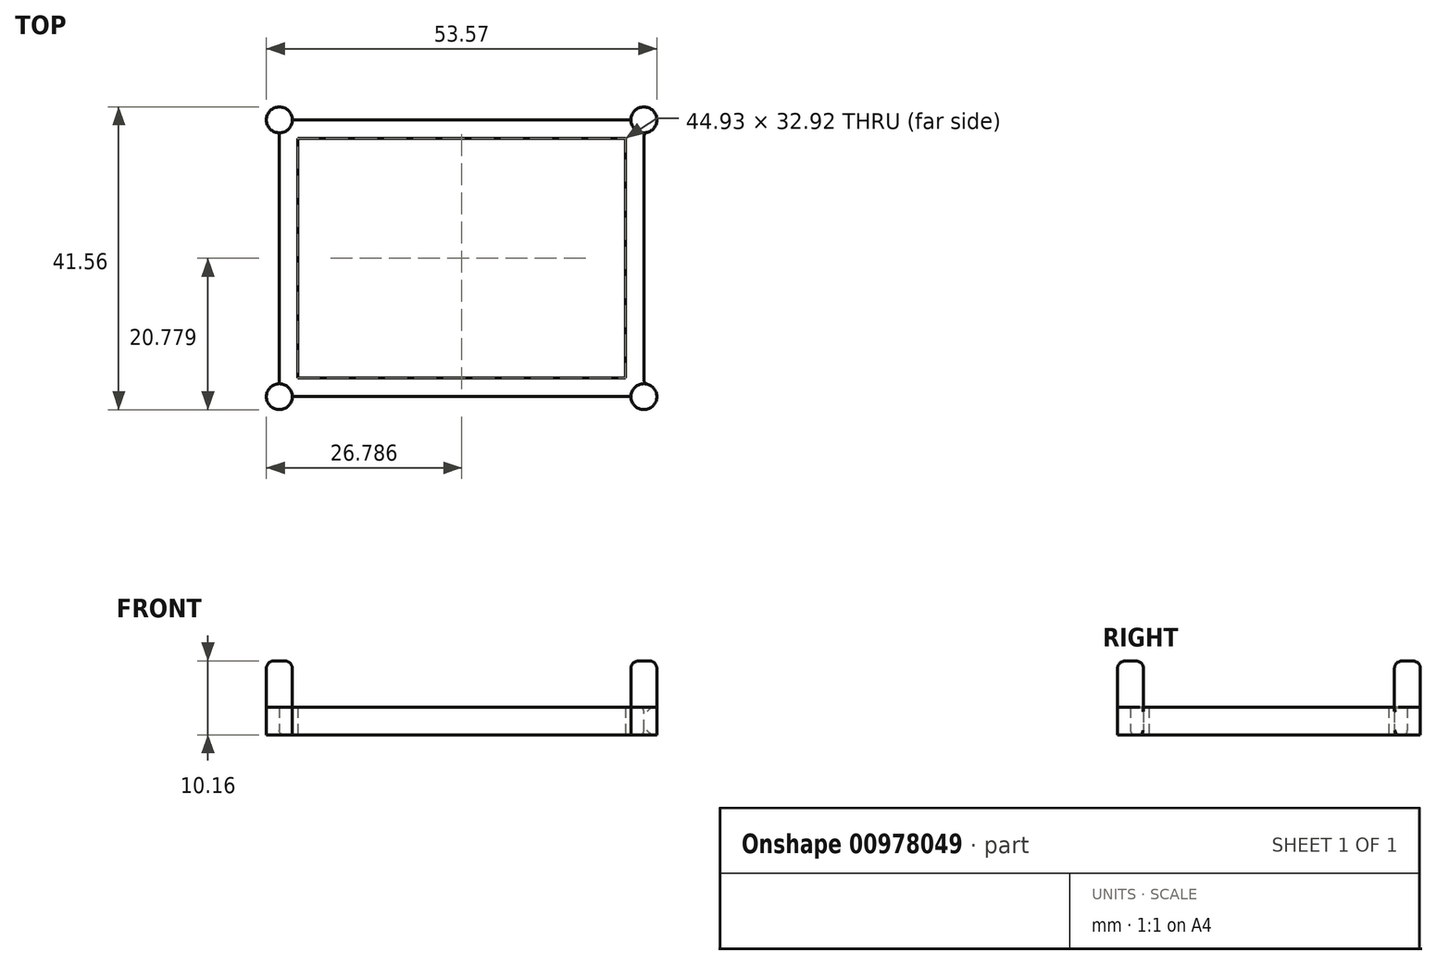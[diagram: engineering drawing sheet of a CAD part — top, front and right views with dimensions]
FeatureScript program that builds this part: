
annotation { "Feature Type Name" : "Feature", "Feature Type Description" : "" }
export const myFeature = defineFeature(function(context is Context, id is Id, definition is map)
    precondition{}
    {
        {
            var Q0;
            Q0=qCreatedBy(makeId("Top.planeOp"),FACE);
            var sketch = newSketch(context, id + "F0", { "sketchPlane" : qUnion([Q0])});
            skLineSegment(sketch, "E0.bottom", {"start": v(0, 0) * mm, "end": v(50.01, 0) * mm});
            skLineSegment(sketch, "E0.top", {"start": v(0, 38) * mm, "end": v(50.01, 38) * mm});
            skLineSegment(sketch, "E0.left", {"start": v(0, 0) * mm, "end": v(0, 38) * mm});
            skLineSegment(sketch, "E0.right", {"start": v(50.01, 0) * mm, "end": v(50.01, 38) * mm});
            skCircle(sketch, "E1", {"center": v(50.01, 38) * mm, "radius": 1.78 * mm});
            skCircle(sketch, "E2", {"center": v(0, 38) * mm, "radius": 1.78 * mm});
            skCircle(sketch, "E3", {"center": v(0, 0) * mm, "radius": 1.78 * mm});
            skCircle(sketch, "E4", {"center": v(50.01, 0) * mm, "radius": 1.78 * mm});
            skSolve(sketch);
        }
        {
            var Q0;
            {var subQ0=sQuery(id+"F0.wireOp",EDGE,"E2");var subQ1=sQuery(id+"F0.wireOp",EDGE,"E0.top");var subQ2=makeQuery(id+"F0.imprint","INTERSECT",VERTEX,{"derivedFrom":[subQ1,subQ0]});Q0=makeQuery(id+"F0.imprint","IMPRINT",FACE,{"disambiguationData":[TD([[makeQuery(id+"F0.imprint","IMPRINT",EDGE,{"disambiguationData":[TD([[subQ2,1.0]])],"derivedFrom":subQ1}),1.0]])]});}
            var Q1;
            {var subQ0=sQuery(id+"F0.wireOp",EDGE,"E2");var subQ1=sQuery(id+"F0.wireOp",EDGE,"E0.top");var subQ2=makeQuery(id+"F0.imprint","INTERSECT",VERTEX,{"derivedFrom":[subQ1,subQ0]});Q1=makeQuery(id+"F0.imprint","IMPRINT",FACE,{"disambiguationData":[TD([[makeQuery(id+"F0.imprint","IMPRINT",EDGE,{"disambiguationData":[TD([[subQ2,1.0]])],"derivedFrom":subQ1}),-1.0]])]});}
            var Q2;
            {var subQ0=sQuery(id+"F0.wireOp",EDGE,"E3");var subQ1=sQuery(id+"F0.wireOp",EDGE,"E0.bottom");var subQ2=makeQuery(id+"F0.imprint","INTERSECT",VERTEX,{"derivedFrom":[subQ1,subQ0]});Q2=makeQuery(id+"F0.imprint","IMPRINT",FACE,{"disambiguationData":[TD([[makeQuery(id+"F0.imprint","IMPRINT",EDGE,{"disambiguationData":[TD([[subQ2,1.0]])],"derivedFrom":subQ1}),-1.0]])]});}
            var Q3;
            {var subQ0=sQuery(id+"F0.wireOp",EDGE,"E3");var subQ1=sQuery(id+"F0.wireOp",EDGE,"E0.bottom");var subQ2=makeQuery(id+"F0.imprint","INTERSECT",VERTEX,{"derivedFrom":[subQ1,subQ0]});Q3=makeQuery(id+"F0.imprint","IMPRINT",FACE,{"disambiguationData":[TD([[makeQuery(id+"F0.imprint","IMPRINT",EDGE,{"disambiguationData":[TD([[subQ2,1.0]])],"derivedFrom":subQ1}),1.0]])]});}
            var Q4;
            {var subQ0=sQuery(id+"F0.wireOp",EDGE,"E0.right");var subQ1=sQuery(id+"F0.wireOp",EDGE,"E0.bottom");var subQ2=makeQuery(id+"F0.imprint","INTERSECT",VERTEX,{"derivedFrom":[subQ1,subQ0]});Q4=makeQuery(id+"F0.imprint","IMPRINT",FACE,{"disambiguationData":[TD([[makeQuery(id+"F0.imprint","IMPRINT",EDGE,{"disambiguationData":[TD([[subQ2,1.0]])],"derivedFrom":subQ1}),1.0]])]});}
            var Q5;
            {var subQ0=sQuery(id+"F0.wireOp",EDGE,"E0.right");var subQ1=sQuery(id+"F0.wireOp",EDGE,"E0.bottom");var subQ2=makeQuery(id+"F0.imprint","INTERSECT",VERTEX,{"derivedFrom":[subQ1,subQ0]});Q5=makeQuery(id+"F0.imprint","IMPRINT",FACE,{"disambiguationData":[TD([[makeQuery(id+"F0.imprint","IMPRINT",EDGE,{"disambiguationData":[TD([[subQ2,1.0]])],"derivedFrom":subQ1}),-1.0]])]});}
            var Q6;
            {var subQ0=sQuery(id+"F0.wireOp",EDGE,"E0.right");var subQ1=sQuery(id+"F0.wireOp",EDGE,"E0.top");var subQ2=makeQuery(id+"F0.imprint","INTERSECT",VERTEX,{"derivedFrom":[subQ1,subQ0]});Q6=makeQuery(id+"F0.imprint","IMPRINT",FACE,{"disambiguationData":[TD([[makeQuery(id+"F0.imprint","IMPRINT",EDGE,{"disambiguationData":[TD([[subQ2,1.0]])],"derivedFrom":subQ1}),-1.0]])]});}
            var Q7;
            {var subQ0=sQuery(id+"F0.wireOp",EDGE,"E0.right");var subQ1=sQuery(id+"F0.wireOp",EDGE,"E0.top");var subQ2=makeQuery(id+"F0.imprint","INTERSECT",VERTEX,{"derivedFrom":[subQ1,subQ0]});Q7=makeQuery(id+"F0.imprint","IMPRINT",FACE,{"disambiguationData":[TD([[makeQuery(id+"F0.imprint","IMPRINT",EDGE,{"disambiguationData":[TD([[subQ2,1.0]])],"derivedFrom":subQ1}),1.0]])]});}
            extrude(context, id + "F1", {"entities" : qUnion([Q0, Q1, Q2, Q3, Q4, Q5, Q6, Q7]), "depth" : 10.16 * mm, "offsetDistance" : 25.4 * mm});
        }
        {
            var Q0;
            Q0 = qSketchRegion(id + "F0", true);
            extrude(context, id + "F2", {"entities" : qUnion([Q0]), "depth" : 3.8 * mm, "offsetDistance" : 25.4 * mm});
        }
        {
            var Q0;
            Q0=makeQuery(id+"F2.opExtrude","CAP_FACE",FACE,{"disambiguationData":[OSD([sQuery(id+"F0.wireOp",EDGE,"E0.bottom"),sQuery(id+"F0.wireOp",EDGE,"E0.top"),sQuery(id+"F0.wireOp",EDGE,"E0.left"),sQuery(id+"F0.wireOp",EDGE,"E0.right"),sQuery(id+"F0.wireOp",EDGE,"E1"),sQuery(id+"F0.wireOp",EDGE,"E2"),sQuery(id+"F0.wireOp",EDGE,"E3"),sQuery(id+"F0.wireOp",EDGE,"E4")])],"isStart":true});
            var sketch = newSketch(context, id + "F3", { "sketchPlane" : qUnion([Q0])});
            skLineSegment(sketch, "E5.bottom", {"start": v(2.54, -2.54) * mm, "end": v(47.47, -2.54) * mm});
            skLineSegment(sketch, "E5.top", {"start": v(2.54, -35.46) * mm, "end": v(47.47, -35.46) * mm});
            skLineSegment(sketch, "E5.left", {"start": v(2.54, -2.54) * mm, "end": v(2.54, -35.46) * mm});
            skLineSegment(sketch, "E5.right", {"start": v(47.47, -2.54) * mm, "end": v(47.47, -35.46) * mm});
            skSolve(sketch);
        }
        {
            var Q0;
            Q0 = qSketchRegion(id + "F3", true);
            extrude(context, id + "F4", {"entities" : qUnion([Q0]), "operationType" : NewBodyOperationType.REMOVE, "oppositeDirection" : true, "depth" : 25.4 * mm, "offsetDistance" : 25.4 * mm});
        }
        {
            var Q0;
            Q0=makeQuery(id+"F1.opExtrude","CAP_EDGE",EDGE,{"disambiguationData":[OSD([sQuery(id+"F0.wireOp",EDGE,"E3")])],"isStart":false});
            var Q1;
            Q1=makeQuery(id+"F1.opExtrude","CAP_EDGE",EDGE,{"disambiguationData":[OSD([sQuery(id+"F0.wireOp",EDGE,"E2")])],"isStart":false});
            var Q2;
            Q2=makeQuery(id+"F1.opExtrude","CAP_EDGE",EDGE,{"disambiguationData":[OSD([sQuery(id+"F0.wireOp",EDGE,"E1")])],"isStart":false});
            var Q3;
            Q3=makeQuery(id+"F1.opExtrude","CAP_EDGE",EDGE,{"disambiguationData":[OSD([sQuery(id+"F0.wireOp",EDGE,"E4")])],"isStart":false});
            fillet(context, id + "F5", {"entities" : qUnion([Q0, Q1, Q2, Q3]), "tangentPropagation" : true, "radius" : 1.04 * mm, "defaultsChanged" : false, "vertexSettings" : [], "allowEdgeOverflow" : false});
        }
        {
            var Q0;
            Q0=makeQuery(id+"F2.opExtrude","CAP_EDGE",EDGE,{"disambiguationData":[OSD([sQuery(id+"F0.wireOp",EDGE,"E0.bottom")])],"isStart":true});
            var Q1;
            Q1=makeQuery(id+"F2.opExtrude","CAP_EDGE",EDGE,{"disambiguationData":[OSD([sQuery(id+"F0.wireOp",EDGE,"E0.left")])],"isStart":true});
            var Q2;
            Q2=makeQuery(id+"F2.opExtrude","CAP_EDGE",EDGE,{"disambiguationData":[OSD([sQuery(id+"F0.wireOp",EDGE,"E0.top")])],"isStart":true});
            var Q3;
            Q3=makeQuery(id+"F2.opExtrude","SWEPT_FACE",FACE,{"disambiguationData":[OSD([sQuery(id+"F0.wireOp",EDGE,"E0.right")])]});
            fillet(context, id + "F6", {"entities" : qUnion([Q0, Q1, Q2, Q3]), "tangentPropagation" : true, "radius" : 0.61 * mm, "defaultsChanged" : false, "vertexSettings" : [], "allowEdgeOverflow" : false});
        }
    });
